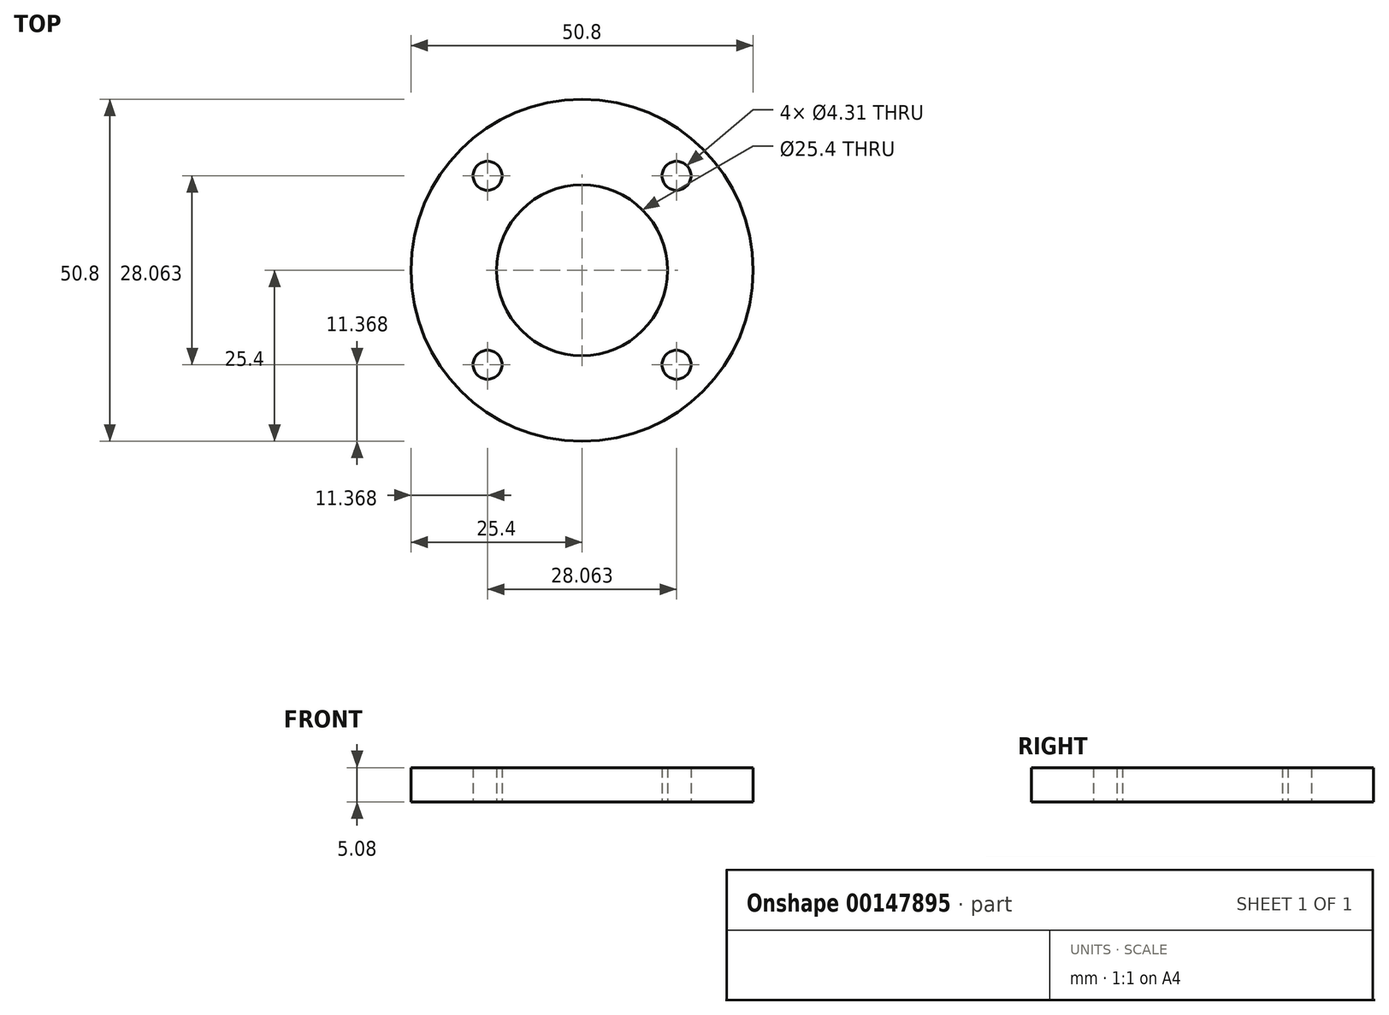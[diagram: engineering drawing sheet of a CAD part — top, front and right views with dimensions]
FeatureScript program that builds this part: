
annotation { "Feature Type Name" : "Feature", "Feature Type Description" : "" }
export const myFeature = defineFeature(function(context is Context, id is Id, definition is map)
    precondition{}
    {
        {
            var Q0;
            Q0=qCreatedBy(makeId("Top.planeOp"),FACE);
            var sketch = newSketch(context, id + "F0", { "sketchPlane" : qUnion([Q0])});
            skCircle(sketch, "E0", {"center": v(0, 0) * mm, "radius": 25.4 * mm});
            skCircle(sketch, "E1", {"center": v(0, 0) * mm, "radius": 14.29 * mm, "construction": true});
            skLineSegment(sketch, "E2.bottom", {"start": v(-14.03, -14.03) * mm, "end": v(14.03, -14.03) * mm, "construction": true});
            skLineSegment(sketch, "E2.top", {"start": v(-14.03, 14.03) * mm, "end": v(14.03, 14.03) * mm, "construction": true});
            skLineSegment(sketch, "E2.left", {"start": v(-14.03, -14.03) * mm, "end": v(-14.03, 14.03) * mm, "construction": true});
            skLineSegment(sketch, "E2.right", {"start": v(14.03, -14.03) * mm, "end": v(14.03, 14.03) * mm, "construction": true});
            skCircle(sketch, "E3", {"center": v(-14.03, -14.03) * mm, "radius": 5.56 * mm, "construction": true});
            skCircle(sketch, "E4", {"center": v(-14.03, -14.03) * mm, "radius": 2.15 * mm});
            skCircle(sketch, "E5", {"center": v(14.03, 14.03) * mm, "radius": 2.15 * mm});
            skCircle(sketch, "E6", {"center": v(14.03, -14.03) * mm, "radius": 2.15 * mm});
            skCircle(sketch, "E7", {"center": v(-14.03, 14.03) * mm, "radius": 2.15 * mm});
            skCircle(sketch, "E8", {"center": v(0, 0) * mm, "radius": 12.7 * mm});
            skSolve(sketch);
        }
        {
            var Q0;
            Q0=makeQuery(id+"F0.imprint","IMPRINT",FACE,{"disambiguationData":[TD([[makeQuery(id+"F0.imprint","IMPRINT",EDGE,{"derivedFrom":sQuery(id+"F0.wireOp",EDGE,"d7zeTPih-CRss-xDOh-gPdP-rmPCdwzH7cdN.left")}),1.0]])]});
            var Q1;
            Q1=makeQuery(id+"F0.imprint","IMPRINT",FACE,{"disambiguationData":[TD([[makeQuery(id+"F0.imprint","IMPRINT",EDGE,{"derivedFrom":sQuery(id+"F0.wireOp",EDGE,"E0")}),1.0]])]});
            extrude(context, id + "F1", {"entities" : qUnion([Q0, Q1]), "depth" : 5.08 * mm});
        }
    });
